# Revit family: IS_TonicII_Multiproduct_BIM_DE_R4341;R4342;R4343;R4344
name_source: partatom
category: Casework
revit_build: Autodesk Revit 2015 (Build: 20140606_1530(x64)
units: mm (PartAtom-declared; Revit-internal decimal feet)

## types (5) — shared parameters
Accessories = www.specifysottini.co.uk
AreaUnits = millimeters
Assembly Code = C1030200
AssetType = Fixed
Brand = Sottini
CodePerformance = FSC, EN 14749:2005
Color = Gloss White
ConnectionType = Mechanical
Default Elevation = 800 mm  [stored 2.62467 ft]
DurationUnit = year
ExpectedLife = 30
Finish = Gloss White
IfcExportAs = IfcFurnitureType
IfcExportType = Shelves
InstallationInstructions = www.idealspec.co.uk/resources.html
LaminateMtl = SOT_Sottini_Laminate_White_Render
LinearUnits = millimeters
MainColor = Gloss White
ManufacturerURL = www.specifysottini.co.uk
Material = Varies, see product information
NBSDescription = Shelves
NBSReference = 45-35-72/354
NominalDepth = 440 mm  [stored 1.44357 ft]
NominalHeight = 170 mm
NominalLength = 440 mm  [stored 1.44357 ft]
Shape = Rectangular
Space = Internal
SpareParts = www.fastpart-spares.co.uk
Style = Shelves
SustainabilityPerformance = FSC
URL = www.specifysottini.co.uk
Uniclass2015Version = Products v1.1
Version = 2
VolumeUnits = Litres
WarrantyDescription = Manufacturers warranty
WarrantyDurationParts = 5
WarrantyDurationUnit = year
zero-valued in all types: Cost

## per-type parameters (varying)
| type | BIMObjectName | Description | Features | Model | ModelNumber | ModelReference | Name | NettWeight | NominalWidth | ProductInformation | Size |
| R4344WG - Turano 450 mm Open Shelf Unit | SOT_Sottini_Shelves_Turano_R4344WG | Turano 450 mm open shelf unit | 450 mm open shelf unit | R4344WG | R4344WG | Turano 450 mm open shelf unit | Shelves_Turano_R4344WG_Sottini | 3.5 Kg | 450 mm  [stored 1.47638 ft] | www.idealspec.co.uk/assets/datasheet/R4344WG | 170 x 440 x 450 mm |
| R4343WG - Turano 800 mm Open Shelf Unit | SOT_Sottini_Shelves_Turano_R4343WG | Turano 800 mm open shelf unit | 800 mm open shelf unit | R4343WG | R4343WG | Turano 800 mm open shelf unit | Shelves_Turano_R4343WG_Sottini | 8 Kg | 800 mm  [stored 2.62467 ft] | www.idealspec.co.uk/assets/datasheet/R4343WG | 170 x 440 x 800 mm |
| R4342WG - Turano 600 mm Open Shelf Unit | SOT_Sottini_Shelves_Turano_R4342WG | Turano 600 mm open shelf unit | 600 mm open shelf unit | R4342WG | R4342WG | Turano 600 mm open shelf unit | Shelves_Turano_R4342WG_Sottini | 7 Kg | 600 mm | www.idealspec.co.uk/assets/datasheet/R4342WG | 170 x 440 x 600 mm |
| R4341WG - Turano 500 mm Open Shelf Unit | SOT_Sottini_Shelves_Turano_R4341WG | Turano 500 mm open shelf unit | 500 mm open shelf unit | R4341WG | R4341WG | Turano 500 mm open shelf unit | Shelves_Turano_R4341WG_Sottini | 5 Kg | 500 mm  [stored 1.64042 ft] | www.idealspec.co.uk/assets/datasheet/R4341WG | 170 x 440 x 500 mm |
| R4340WG - Turano 350 mm Open Shelf Unit | SOT_Sottini_Shelves_Turano_R4340WG | Turano 350 mm open shelf unit | 350 mm open shelf unit | R4340WG | R4340WG | Turano 350 mm open shelf unit | Shelves_Turano_R4340WG_Sottini | 5 Kg | 350 mm | www.idealspec.co.uk/assets/datasheet/R4340WG | 170 x 440 x 351 mm |

note: [stored X ft] marks values corroborated as IEEE doubles in the binary element streams (Revit-internal decimal feet)

## geometry (parser evidence)
native form markers: Blend x2, Sweep x3
no freeform markers — native parametric forms only
